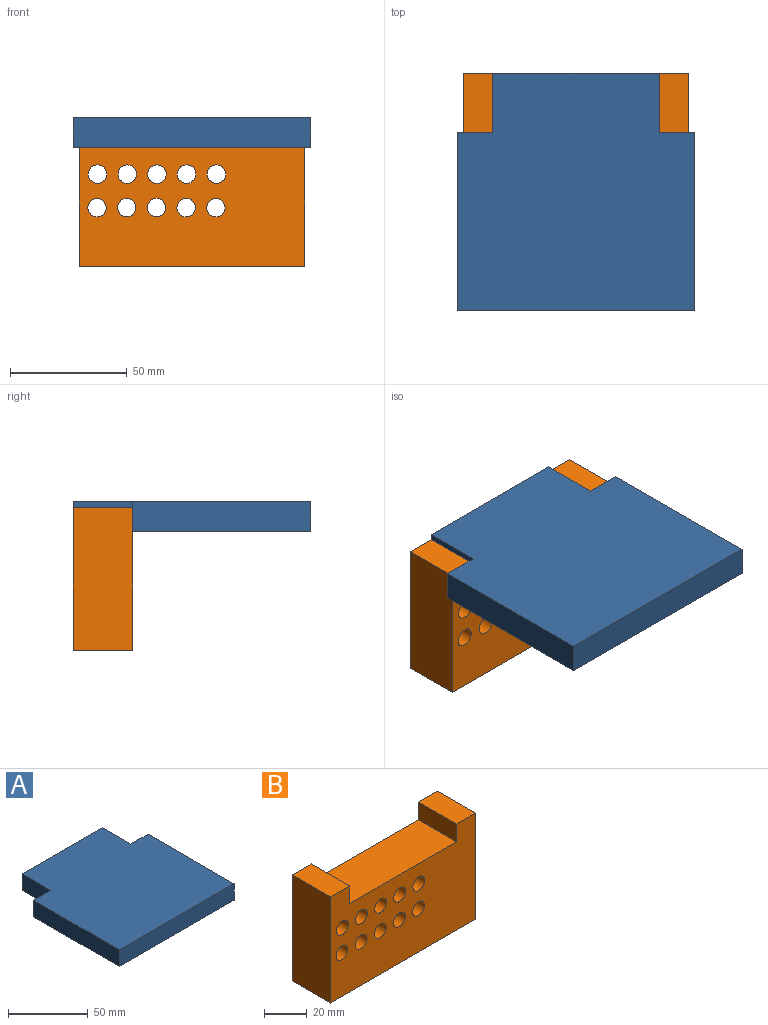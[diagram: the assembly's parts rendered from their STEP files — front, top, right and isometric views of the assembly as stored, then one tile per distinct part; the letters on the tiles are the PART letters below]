
ASSEMBLY  parts=2 mates=1
PART A: 10 faces, bbox 101.6x101.6x12.7 mm
  f0: plane 71.12x12.7mm, normal (0,1,0), area 903.2mm2, adj f1,f7,f8,f9
  f1: plane 25.4x12.7mm, normal (-1,0,0), area 322.6mm2, adj f0,f2,f8,f9
  f2: plane 15.24x12.7mm, normal (0,1,0), area 193.5mm2, adj f1,f3,f8,f9
  f3: plane 76.2x12.7mm, normal (-1,0,0), area 967.7mm2, adj f2,f4,f8,f9
  f4: plane 101.6x12.7mm, normal (0,-1,0), area 1290.3mm2, adj f3,f5,f8,f9
  f5: plane 76.2x12.7mm, normal (1,0,0), area 967.7mm2, adj f4,f6,f8,f9
  f6: plane 15.24x12.7mm, normal (0,1,0), area 193.5mm2, adj f5,f7,f8,f9
  f7: plane 25.4x12.7mm, normal (1,0,0), area 322.6mm2, adj f0,f6,f8,f9
  f8: plane 101.6x101.6mm, normal (0,0,1), area 9548.4mm2, adj f0,f1,f2,f3,f4,f5,f6,f7
  f9: plane 101.6x101.6mm, normal (0,0,-1), area 9548.4mm2, adj f0,f1,f2,f3,f4,f5,f6,f7
PART B: 20 faces, bbox 96.5x25.4x61 mm
  f0: plane 25.4x10.16mm, normal (-1,0,0), area 258.1mm2, adj f1,f16,f18,f19
  f1: plane 71.12x25.4mm, normal (0,0,1), area 1806.4mm2, adj f0,f2,f18,f19
  f2: plane 25.4x10.16mm, normal (1,0,0), area 258.1mm2, adj f1,f3,f18,f19
  f3: plane 25.4x12.7mm, normal (0,0,1), area 322.6mm2, adj f2,f4,f18,f19
  f4: plane 60.96x25.4mm, normal (-1,0,0), area 1548.4mm2, adj f3,f5,f18,f19
  f5: plane 96.52x25.4mm, normal (0,0,-1), area 2451.6mm2, adj f4,f6,f18,f19
  f6: plane 60.96x25.4mm, normal (1,0,0), area 1548.4mm2, adj f5,f16,f18,f19
  f7: cylinder r=3.94mm len=25.4mm, axis (0,1,0), area 628.1mm2, adj f18,f19
  f8: cylinder r=3.94mm len=25.4mm, axis (0,1,0), area 628.1mm2, adj f18,f19
  f9: cylinder r=3.94mm len=25.4mm, axis (0,1,0), area 628.1mm2, adj f18,f19
  f10: cylinder r=3.94mm len=25.4mm, axis (0,1,0), area 628.1mm2, adj f18,f19
  f11: cylinder r=3.94mm len=25.4mm, axis (0,1,0), area 628.1mm2, adj f18,f19
  f12: cylinder r=3.94mm len=25.4mm, axis (0,1,0), area 628.1mm2, adj f18,f19
  f13: cylinder r=3.94mm len=25.4mm, axis (0,1,0), area 628.1mm2, adj f18,f19
  f14: cylinder r=3.94mm len=25.4mm, axis (0,1,0), area 628.1mm2, adj f18,f19
  f15: cylinder r=3.94mm len=25.4mm, axis (0,1,0), area 628.1mm2, adj f18,f19
  f16: plane 25.4x12.7mm, normal (0,0,1), area 322.6mm2, adj f0,f6,f18,f19
  f17: cylinder r=3.94mm len=25.4mm, axis (0,1,0), area 628.1mm2, adj f18,f19
  f18: plane 96.52x60.96mm, normal (0,-1,0), area 4674.6mm2, adj f0,f1,f2,f3,f4,f5,f6,f7
  f19: plane 96.52x60.96mm, normal (0,1,0), area 4674.6mm2, adj f0,f1,f2,f3,f4,f5,f6,f7
PLACE A t=(-34.66,-130.29,-56.18)mm
PLACE B t=(-34.66,-79.49,-106.98)mm
MATE fastened A.f9 <-> B.f1  axis (0,0,-1) through (-34.66,-79.49,-56.18)mm
